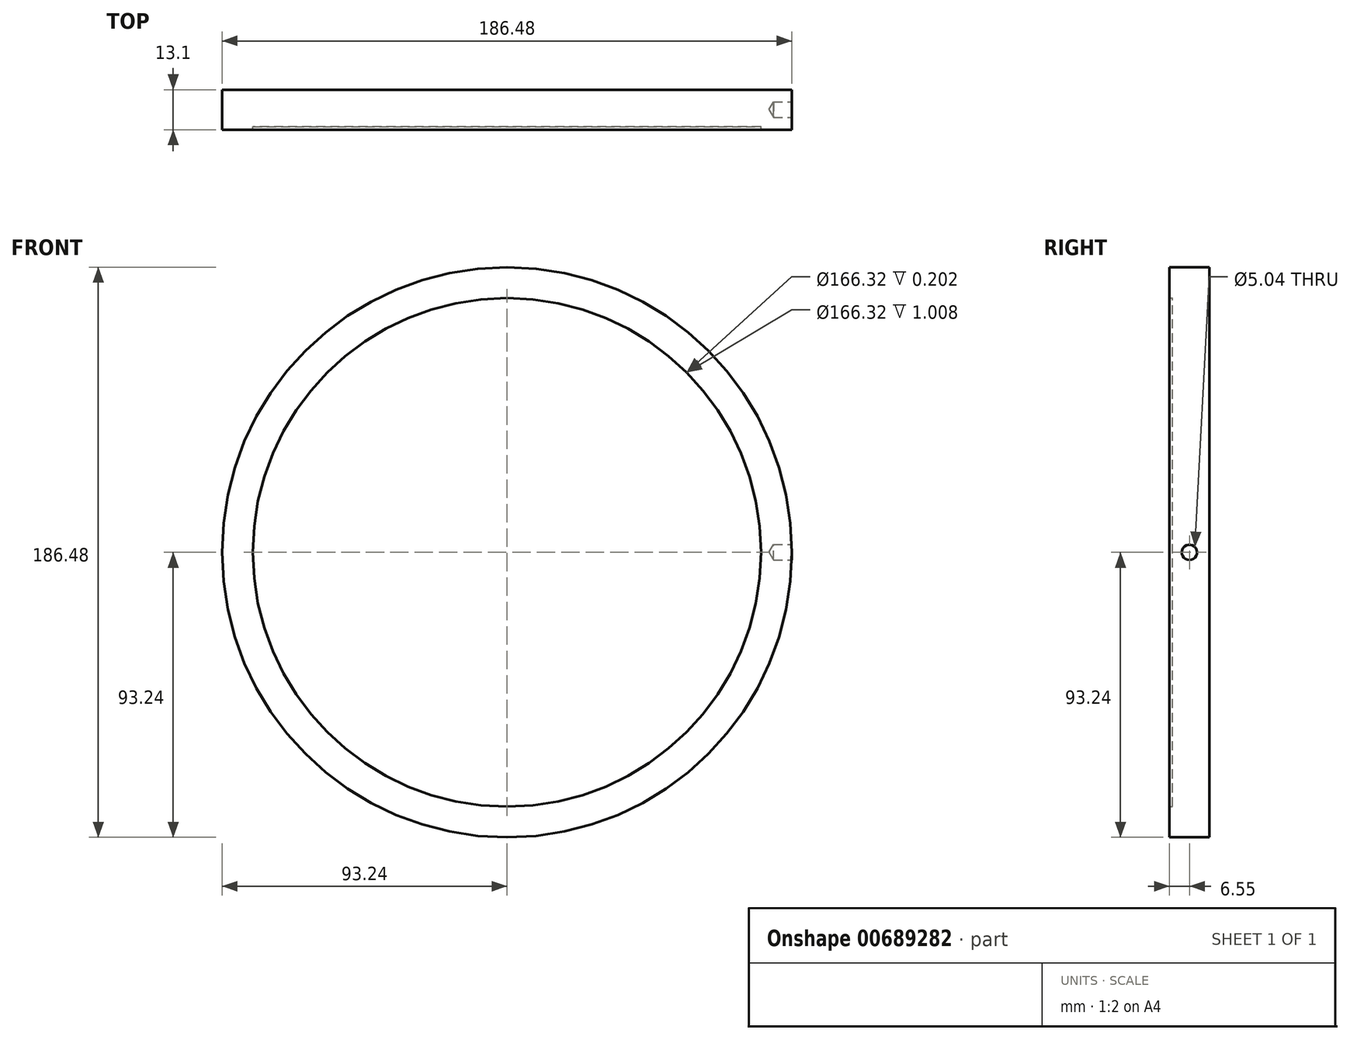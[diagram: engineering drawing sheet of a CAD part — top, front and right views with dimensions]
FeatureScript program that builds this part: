
annotation { "Feature Type Name" : "Feature", "Feature Type Description" : "" }
export const myFeature = defineFeature(function(context is Context, id is Id, definition is map)
    precondition{}
    {
        {
            var Q0;
            Q0=qCreatedBy(makeId("Front.planeOp"),FACE);
            var sketch = newSketch(context, id + "F0", { "sketchPlane" : qUnion([Q0])});
            skCircle(sketch, "E0", {"center": v(0, 0) * mm, "radius": 82.5 * mm});
            skCircle(sketch, "E1", {"center": v(0, 0) * mm, "radius": 92.5 * mm});
            skSolve(sketch);
        }
        {
            var Q0;
            Q0=makeQuery(id+"F0.imprint","IMPRINT",FACE,{"disambiguationData":[TD([[makeQuery(id+"F0.imprint","IMPRINT",EDGE,{"derivedFrom":sQuery(id+"F0.wireOp",EDGE,"E0")}),-1.0]])]});
            extrude(context, id + "F1", {"entities" : qUnion([Q0]), "endBound" : BoundingType.SYMMETRIC, "depth" : 13 * mm, "offsetDistance" : 25 * mm});
        }
        {
            var Q0;
            Q0=makeQuery(id+"F0.imprint","IMPRINT",FACE,{"disambiguationData":[TD([[makeQuery(id+"F0.imprint","IMPRINT",EDGE,{"derivedFrom":sQuery(id+"F0.wireOp",EDGE,"E0")}),1.0]])]});
            extrude(context, id + "F2", {"entities" : qUnion([Q0]), "operationType" : NewBodyOperationType.ADD, "endBound" : BoundingType.SYMMETRIC, "depth" : 11 * mm, "offsetDistance" : 25 * mm});
        }
        {
            var Q0;
            Q0=makeQuery(id+"F2.opExtrude","CAP_FACE",FACE,{"disambiguationData":[OSD([sQuery(id+"F0.wireOp",EDGE,"E0")])],"isStart":true});
            extrude(context, id + "F3", {"entities" : qUnion([Q0]), "operationType" : NewBodyOperationType.ADD, "depth" : .8 * mm, "offsetDistance" : 25 * mm});
        }
        {
            var Q0;
            Q0=qCreatedBy(makeId("Front.planeOp"),FACE);
            var sketch = newSketch(context, id + "F4", { "sketchPlane" : qUnion([Q0])});
            skArc(sketch, "E2.0", {"start": v(92.5, 0) * mm, "mid": v(92.5, 1.25) * mm, "end": v(92.47, 2.5) * mm});
            skLineSegment(sketch, "E3", {"start": v(85.06, 0) * mm, "end": v(92.5, 0) * mm});
            skLineSegment(sketch, "E4", {"start": v(92.5, 0) * mm, "end": v(92.5, 2.5) * mm});
            skLineSegment(sketch, "E5", {"start": v(92.5, 2.5) * mm, "end": v(86.5, 2.5) * mm});
            skLineSegment(sketch, "E6", {"start": v(86.5, 2.5) * mm, "end": v(85.06, 0) * mm});
            skSolve(sketch);
        }
        {
            var Q0;
            Q0 = qSketchRegion(id + "F4", true);
            var Q1;
            Q1=sQuery(id+"F4.wireOp",EDGE,"E3");
            revolve(context, id + "F5", {"operationType" : NewBodyOperationType.REMOVE, "entities" : qUnion([Q0]), "axis" : qUnion([Q1]), "revolveType" : RevolveType.FULL, "oppositeDirection" : true});
        }
        {
            var Q0;
            Q0=makeQuery(id+"F1.opExtrude","SWEPT_BODY",BODY,{"disambiguationData":[OSD([sQuery(id+"F0.wireOp",EDGE,"E0"),sQuery(id+"F0.wireOp",EDGE,"E1")])]});
            var Q1;
            Q1=qCreatedBy(makeId("Origin.pointOp"),VERTEX);
            transform(context, id + "F6", {"entities" : qUnion([Q0]), "transformType" : TransformType.SCALE_UNIFORMLY, "scale" : 1, "scalePoint" : qUnion([Q1]), "makeCopy" : false});
        }
        {
            var Q0;
            Q0=makeQuery(id+"F1.opExtrude","SWEPT_BODY",BODY,{"disambiguationData":[OSD([sQuery(id+"F0.wireOp",EDGE,"E0"),sQuery(id+"F0.wireOp",EDGE,"E1")])]});
            var Q1;
            Q1=qCreatedBy(makeId("Origin.pointOp"),VERTEX);
            transform(context, id + "F7", {"entities" : qUnion([Q0]), "transformType" : TransformType.SCALE_UNIFORMLY, "scale" : 1, "scalePoint" : qUnion([Q1]), "makeCopy" : false});
        }
        {
            var Q0;
            Q0=makeQuery(id+"F1.opExtrude","SWEPT_BODY",BODY,{"disambiguationData":[OSD([sQuery(id+"F0.wireOp",EDGE,"E0"),sQuery(id+"F0.wireOp",EDGE,"E1")])]});
            var Q1;
            Q1=qCreatedBy(makeId("Origin.pointOp"),VERTEX);
            transform(context, id + "F8", {"entities" : qUnion([Q0]), "transformType" : TransformType.SCALE_UNIFORMLY, "scale" : .998, "scalePoint" : qUnion([Q1]), "makeCopy" : false});
        }
    });
